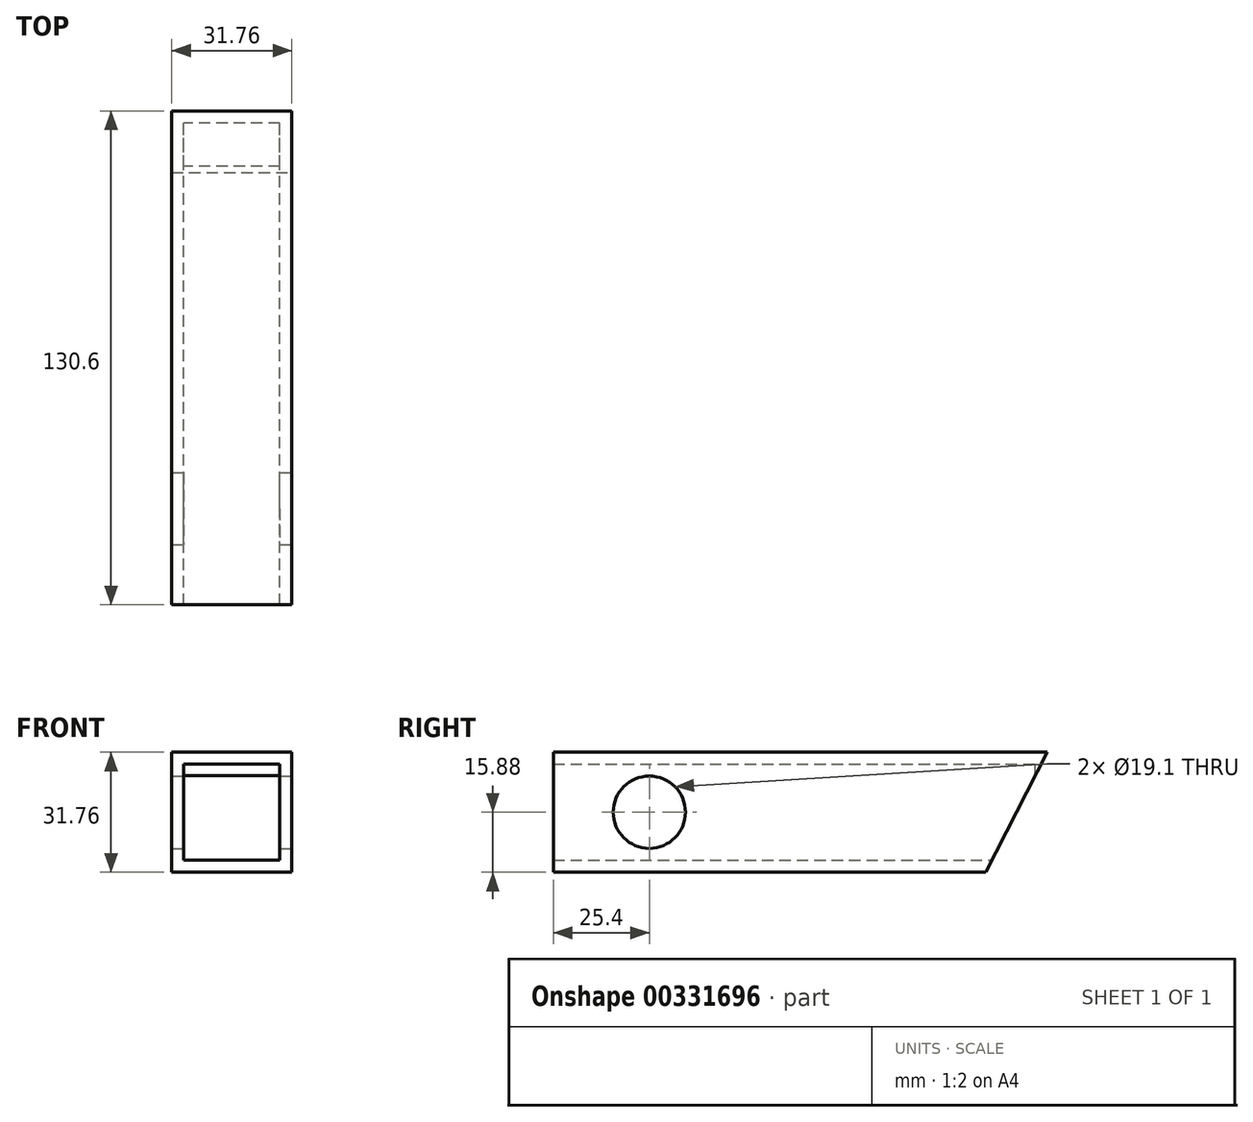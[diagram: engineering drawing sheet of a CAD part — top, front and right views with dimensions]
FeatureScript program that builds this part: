
annotation { "Feature Type Name" : "Feature", "Feature Type Description" : "" }
export const myFeature = defineFeature(function(context is Context, id is Id, definition is map)
    precondition{}
    {
        {
            var Q0;
            Q0=qCreatedBy(makeId("Front.planeOp"),FACE);
            var sketch = newSketch(context, id + "F0", { "sketchPlane" : qUnion([Q0])});
            skLineSegment(sketch, "E0.bottom", {"start": v(15.88, -15.87) * mm, "end": v(-15.88, -15.88) * mm});
            skLineSegment(sketch, "E0.top", {"start": v(15.88, 15.88) * mm, "end": v(-15.88, 15.87) * mm});
            skLineSegment(sketch, "E0.left", {"start": v(15.88, -15.88) * mm, "end": v(15.88, 15.88) * mm});
            skLineSegment(sketch, "E0.right", {"start": v(-15.88, -15.88) * mm, "end": v(-15.88, 15.88) * mm});
            skPoint(sketch, "E0.middle", {"position": v(0, 0) * mm});
            skSolve(sketch);
        }
        {
            var Q0;
            Q0=makeQuery(id+"F0.imprint","IMPRINT",FACE,{"disambiguationData":[TD([[makeQuery(id+"F0.imprint","IMPRINT",EDGE,{"derivedFrom":sQuery(id+"F0.wireOp",EDGE,"E0.bottom")}),-1.0]])]});
            extrude(context, id + "F1", {"entities" : qUnion([Q0]), "depth" : 130.6 * mm});
        }
        {
            var Q0;
            Q0=makeQuery(id+"F1.opExtrude","CAP_FACE",FACE,{"disambiguationData":[OSD([sQuery(id+"F0.wireOp",EDGE,"E0.bottom"),sQuery(id+"F0.wireOp",EDGE,"E0.top"),sQuery(id+"F0.wireOp",EDGE,"E0.left"),sQuery(id+"F0.wireOp",EDGE,"E0.right")])],"isStart":false});
            shell(context, id + "F2", {"entities" : qUnion([Q0]), "thickness" : 3.17 * mm});
        }
        {
            var Q0;
            Q0=makeQuery(id+"F1.opExtrude","SWEPT_FACE",FACE,{"disambiguationData":[OSD([sQuery(id+"F0.wireOp",EDGE,"E0.left")])]});
            var sketch = newSketch(context, id + "F3", { "sketchPlane" : qUnion([Q0])});
            skLineSegment(sketch, "E1", {"start": v(0, 15.88) * mm, "end": v(-16.3, -15.88) * mm});
            skPoint(sketch, "E2", {"position": v(-105.2, 0) * mm});
            skSolve(sketch);
        }
        {
            var Q0;
            {var subQ0=sQuery(id+"F3.wireOp",EDGE,"E1");Q0=makeQuery(id+"F3.imprint","IMPRINT",FACE,{"disambiguationData":[TD([[makeQuery(id+"F3.imprint","IMPRINT",EDGE,{"derivedFrom":subQ0}),1.0]])]});}
            extrude(context, id + "F4", {"entities" : qUnion([Q0]), "operationType" : NewBodyOperationType.REMOVE, "oppositeDirection" : true, "depth" : 50.8 * mm});
        }
        {
            var Q0;
            Q0=sQuery(id+"F3.wireOp",VERTEX,"E2");
            var Q1;
            Q1=makeQuery(id+"F1.opExtrude","SWEPT_BODY",BODY,{"disambiguationData":[OSD([sQuery(id+"F0.wireOp",EDGE,"E0.bottom"),sQuery(id+"F0.wireOp",EDGE,"E0.top"),sQuery(id+"F0.wireOp",EDGE,"E0.left"),sQuery(id+"F0.wireOp",EDGE,"E0.right")])]});
            hole(context, id + "F5", {"style" : HoleStyle.SIMPLE, "endStyle" : HoleEndStyle.THROUGH, "holeDiameter" : 19.1 * mm, "tappedDepth" : 19.38 * mm, "tapClearance" : 3, "startFromSketch" : true, "locations" : qUnion([Q0]), "scope" : qUnion([Q1])});
        }
    });
